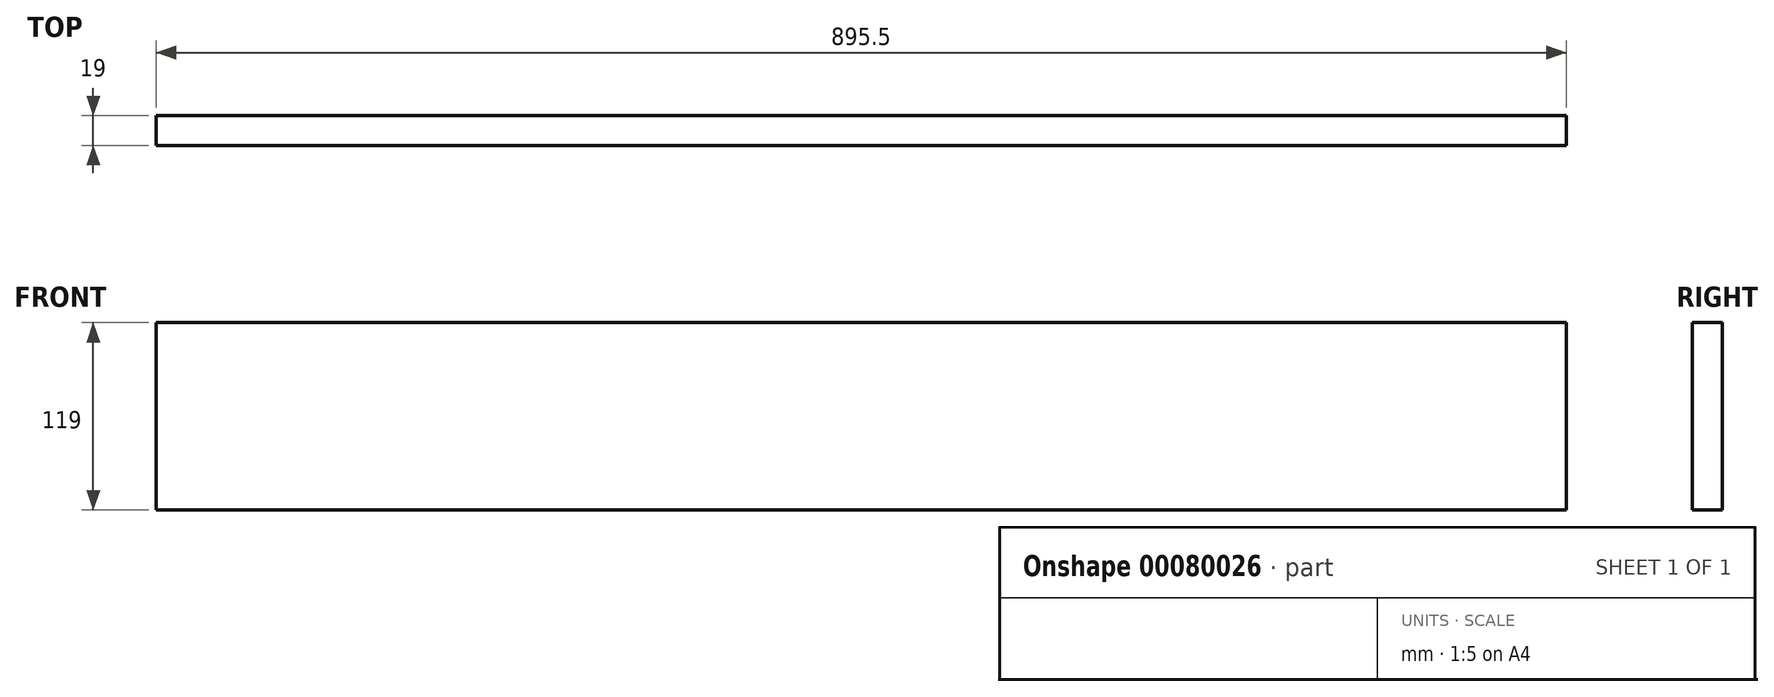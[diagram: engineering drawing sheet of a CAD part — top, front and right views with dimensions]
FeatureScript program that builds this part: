
annotation { "Feature Type Name" : "Feature", "Feature Type Description" : "" }
export const myFeature = defineFeature(function(context is Context, id is Id, definition is map)
    precondition{}
    {
        {
            var Q0;
            Q0=qCreatedBy(makeId("Front.planeOp"),FACE);
            var sketch = newSketch(context, id + "F0", { "sketchPlane" : qUnion([Q0])});
            skLineSegment(sketch, "E0.bottom", {"start": v(0, 0) * mm, "end": v(895.5, 0) * mm});
            skLineSegment(sketch, "E0.top", {"start": v(0, -119) * mm, "end": v(895.5, -119) * mm});
            skLineSegment(sketch, "E0.left", {"start": v(0, 0) * mm, "end": v(0, -119) * mm});
            skLineSegment(sketch, "E0.right", {"start": v(895.5, 0) * mm, "end": v(895.5, -119) * mm});
            skSolve(sketch);
        }
        {
            var Q0;
            Q0 = qSketchRegion(id + "F0", true);
            extrude(context, id + "F1", {"entities" : qUnion([Q0]), "depth" : 19 * mm});
        }
    });
